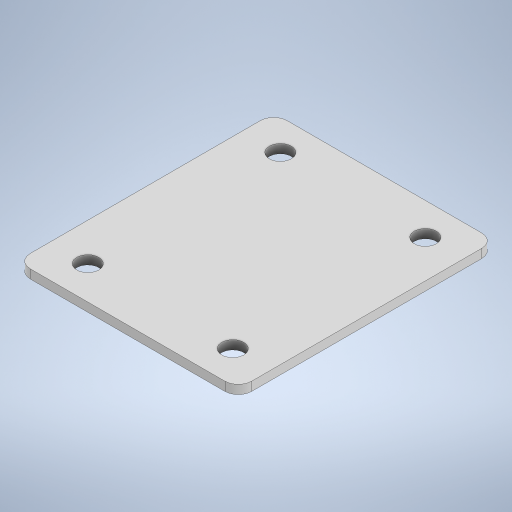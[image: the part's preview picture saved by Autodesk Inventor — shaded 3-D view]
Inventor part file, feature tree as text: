
AUTODESK INVENTOR PART (.ipt)
format: ipt  version: 2024.2 (Build 282272000, 272)  size: 237,056 bytes
history: native  units: mm
features: extrude x1, fillet x1, sketch x1
ambient origin geometry x8: Origin, YZ Plane, XZ Plane, XY Plane, X Axis, Y Axis, Z Axis, Center Point
bodies: Solid1 (feature_tree)
feature tree (3):
  extrude  "Extrusion1"  Depth=58.0mm
  fillet  "Fillet1"  Radius=5.0mm
  sketch  "Sketch1"  dims[d0=50.0mm d1=58.0mm d2=5.0mm d3=5.0mm d4=5.0mm d5=5.0mm d7=8.5mm d8=33.0mm d9=33.0mm d10=7.25mm d11=7.0mm d14=43.5mm d15=43.5mm d16=2.0mm d17=0.0mm d18=3.0mm d19=0.0mm d20=0.0mm d21=0.0mm]
